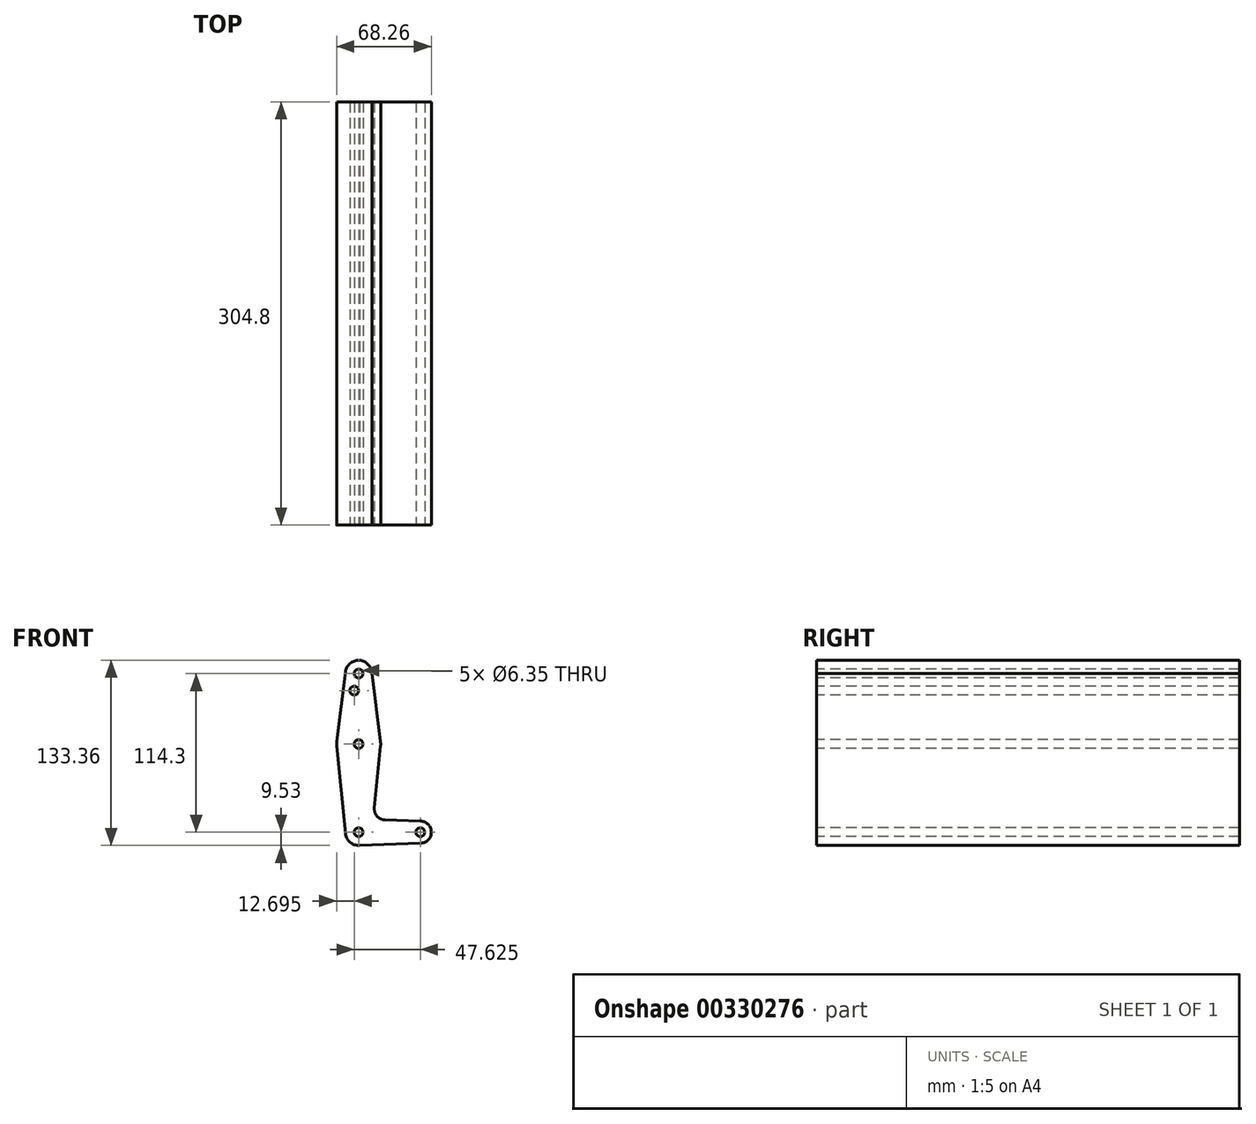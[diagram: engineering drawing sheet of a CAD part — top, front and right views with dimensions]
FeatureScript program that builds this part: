
annotation { "Feature Type Name" : "Feature", "Feature Type Description" : "" }
export const myFeature = defineFeature(function(context is Context, id is Id, definition is map)
    precondition{}
    {
        {
            var Q0;
            Q0=qCreatedBy(makeId("Front.planeOp"),FACE);
            var sketch = newSketch(context, id + "F0", { "sketchPlane" : qUnion([Q0])});
            skLineSegment(sketch, "E0", {"start": v(0, 0) * mm, "end": v(0, 114.3) * mm, "construction": true});
            skLineSegment(sketch, "E1", {"start": v(0, 0) * mm, "end": v(44.45, 0) * mm, "construction": true});
            skCircle(sketch, "E2", {"center": v(0, 114.3) * mm, "radius": 9.53 * mm});
            skCircle(sketch, "E3", {"center": v(0, 0) * mm, "radius": 9.53 * mm});
            skCircle(sketch, "E4", {"center": v(44.45, 0) * mm, "radius": 7.94 * mm});
            skCircle(sketch, "E5", {"center": v(0, 63.5) * mm, "radius": 15.88 * mm});
            skLineSegment(sketch, "E6", {"start": v(9.53, 114.3) * mm, "end": v(15.75, 65.5) * mm});
            skLineSegment(sketch, "E7", {"start": v(-9.45, 115.5) * mm, "end": v(-15.75, 65.48) * mm});
            skLineSegment(sketch, "E8", {"start": v(0, -9.52) * mm, "end": v(44.73, -7.93) * mm});
            skLineSegment(sketch, "E9", {"start": v(18.97, 8.85) * mm, "end": v(44.73, 7.93) * mm});
            skCircle(sketch, "E10", {"center": v(0, 114.3) * mm, "radius": 3.18 * mm});
            skCircle(sketch, "E11", {"center": v(44.45, 0) * mm, "radius": 3.18 * mm});
            skCircle(sketch, "E12", {"center": v(0, 0) * mm, "radius": 3.18 * mm});
            skCircle(sketch, "E13", {"center": v(0, 63.5) * mm, "radius": 3.17 * mm});
            skLineSegment(sketch, "E14", {"start": v(-15.8, 61.91) * mm, "end": v(-9.48, -0.95) * mm});
            skLineSegment(sketch, "E15", {"start": v(15.8, 61.91) * mm, "end": v(11.34, 17.59) * mm});
            skCircle(sketch, "E16", {"center": v(-3.18, 102) * mm, "radius": 3.18 * mm});
            skPoint(sketch, "E17.newPointB", {"position": v(9.48, -0.95) * mm});
            skArc(sketch, "E17.filletArc", {"start": v(11.34, 17.59) * mm, "mid": v(13.26, 11.57) * mm, "end": v(18.97, 8.85) * mm});
            skSolve(sketch);
        }
        {
            var Q0;
            Q0 = qSketchRegion(id + "F0", true);
            extrude(context, id + "F1", {"entities" : qUnion([Q0]), "oppositeDirection" : true, "depth" : 304.8 * mm});
        }
    });
